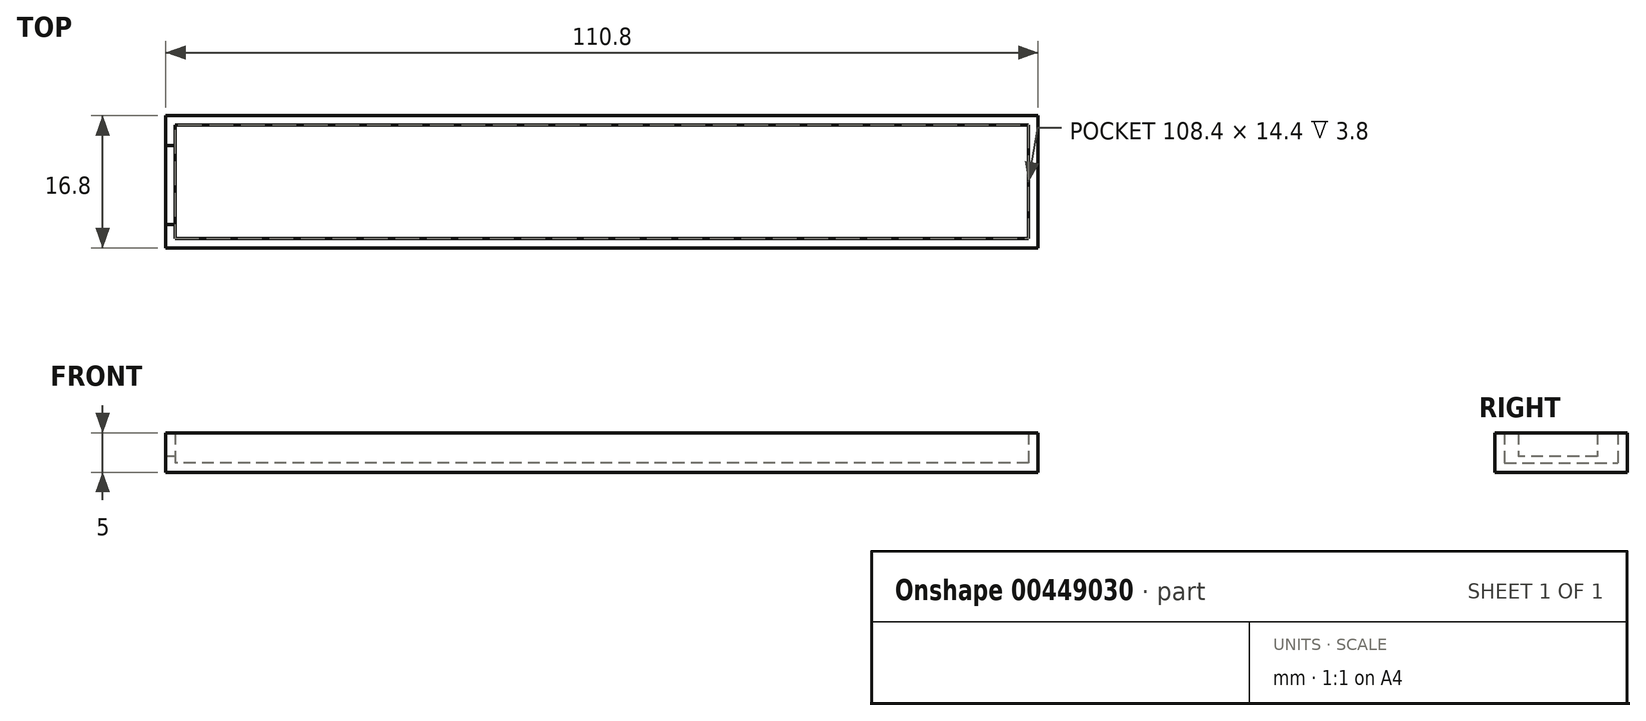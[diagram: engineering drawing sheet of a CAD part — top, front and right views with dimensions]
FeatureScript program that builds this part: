
annotation { "Feature Type Name" : "Feature", "Feature Type Description" : "" }
export const myFeature = defineFeature(function(context is Context, id is Id, definition is map)
    precondition{}
    {
        {
            var Q0;
            Q0=qCreatedBy(makeId("Top.planeOp"),FACE);
            var sketch = newSketch(context, id + "F0", { "sketchPlane" : qUnion([Q0])});
            skLineSegment(sketch, "E0.bottom", {"start": v(55, -8) * mm, "end": v(-55, -8) * mm});
            skLineSegment(sketch, "E0.top", {"start": v(55, 8) * mm, "end": v(-55, 8) * mm});
            skLineSegment(sketch, "E0.left", {"start": v(55, -8) * mm, "end": v(55, 8) * mm});
            skLineSegment(sketch, "E0.right", {"start": v(-55, -8) * mm, "end": v(-55, 8) * mm});
            skPoint(sketch, "E0.middle", {"position": v(0, 0) * mm});
            skLineSegment(sketch, "E1.0", {"start": v(55.4, 8.4) * mm, "end": v(-55.4, 8.4) * mm});
            skLineSegment(sketch, "E1.1", {"start": v(55.4, -8.4) * mm, "end": v(55.4, 8.4) * mm});
            skLineSegment(sketch, "E1.2", {"start": v(55.4, -8.4) * mm, "end": v(-55.4, -8.4) * mm});
            skLineSegment(sketch, "E1.3", {"start": v(-55.4, -8.4) * mm, "end": v(-55.4, 8.4) * mm});
            skSolve(sketch);
        }
        {
            var Q0;
            Q0=makeQuery(id+"F0.imprint","IMPRINT",FACE,{"disambiguationData":[TD([[makeQuery(id+"F0.imprint","IMPRINT",EDGE,{"derivedFrom":sQuery(id+"F0.wireOp",EDGE,"E0.bottom")}),1.0]])]});
            var Q1;
            Q1=makeQuery(id+"F0.imprint","IMPRINT",FACE,{"disambiguationData":[TD([[makeQuery(id+"F0.imprint","IMPRINT",EDGE,{"derivedFrom":sQuery(id+"F0.wireOp",EDGE,"E0.bottom")}),-1.0]])]});
            extrude(context, id + "F1", {"entities" : qUnion([Q0, Q1]), "depth" : 5 * mm, "offsetDistance" : 25 * mm});
        }
        {
            var Q0;
            Q0=makeQuery(id+"F1.opExtrude","CAP_FACE",FACE,{"disambiguationData":[OSD([sQuery(id+"F0.wireOp",EDGE,"E1.0"),sQuery(id+"F0.wireOp",EDGE,"E1.1"),sQuery(id+"F0.wireOp",EDGE,"E1.2"),sQuery(id+"F0.wireOp",EDGE,"E1.3")])],"isStart":false});
            shell(context, id + "F2", {"entities" : qUnion([Q0]), "thickness" : 1.2 * mm});
        }
        {
            var Q0;
            Q0=makeQuery(id+"F1.opExtrude","SWEPT_FACE",FACE,{"disambiguationData":[OSD([sQuery(id+"F0.wireOp",EDGE,"E1.3")])]});
            cPlane(context, id + "F3", {"entities" : qUnion([Q0]), "cplaneType" : CPlaneType.OFFSET, "offset" : 0 * mm, "width" : 150 * mm, "height" : 150 * mm});
        }
        {
            var Q0;
            Q0=qCreatedBy(id+"F3.planeOp",FACE);
            var sketch = newSketch(context, id + "F4", { "sketchPlane" : qUnion([Q0])});
            skLineSegment(sketch, "E2.bottom", {"start": v(-4.6, 5) * mm, "end": v(5.4, 5) * mm});
            skLineSegment(sketch, "E2.top", {"start": v(-4.6, 2) * mm, "end": v(5.4, 2) * mm});
            skLineSegment(sketch, "E2.left", {"start": v(-4.6, 5) * mm, "end": v(-4.6, 2) * mm});
            skLineSegment(sketch, "E2.right", {"start": v(5.4, 5) * mm, "end": v(5.4, 2) * mm});
            skSolve(sketch);
        }
        {
            var Q0;
            Q0=makeQuery(id+"F4.imprint","IMPRINT",FACE,{"disambiguationData":[TD([[makeQuery(id+"F4.imprint","IMPRINT",EDGE,{"derivedFrom":sQuery(id+"F4.wireOp",EDGE,"E2.bottom")}),-1.0]])]});
            extrude(context, id + "F5", {"entities" : qUnion([Q0]), "operationType" : NewBodyOperationType.REMOVE, "oppositeDirection" : true, "depth" : 2 * mm, "offsetDistance" : 25 * mm});
        }
    });
